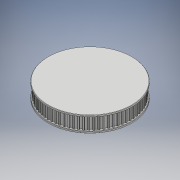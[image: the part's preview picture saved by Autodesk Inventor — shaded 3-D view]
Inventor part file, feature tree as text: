
AUTODESK INVENTOR PART (.ipt)
format: ipt  version: 2018 (Build 220112000, 112)  size: 691,712 bytes
history: native  units: mm
features: extrude x4, sketch x3, other x1, pattern_circular x1, fillet x1
ambient origin geometry x8: Origin, YZ Plane, XZ Plane, XY Plane, X Axis, Y Axis, Z Axis, Center Point
bodies: Solid1 (feature_tree)
feature tree (10):
  other  "Tooth"
  extrude  "Gear Solid Extrusion"  Depth=1.5mm
  extrude  "Tooth Cut-Out Extrusion"  Depth=0.85mm
  pattern_circular  "Teeth Array"  [2 undecoded]
  extrude  "Flange Extrusion Front"  Depth=0.25mm
  extrude  "Flange Extrusion Back"  Depth=33.422538mm
  fillet  "Flange Fillet"  [1 undecoded]
  sketch  "Sketch2"  dims[d2=33.422538mm d3=1.5mm]
  sketch  "Sketch3"  dims[d4=1.14mm d5=0.85mm]
  sketch  "Sketch4"  dims[d6=0.61mm d7=0.25mm d8=2.0mm d9=33.422538mm d11=0.0mm d12=10.0mm d13=0.0mm d14=700.0mm d15=360.0deg d17=34.422538mm d19=0.0mm d20=34.422538mm d21=1.5mm d22=0.0mm d23=0.25mm]
note: 3 required parameter values undecoded (feature->parameter linkage not recoverable at this tier; creation-order binding heuristic only, values carry confidence <= 0.55)
